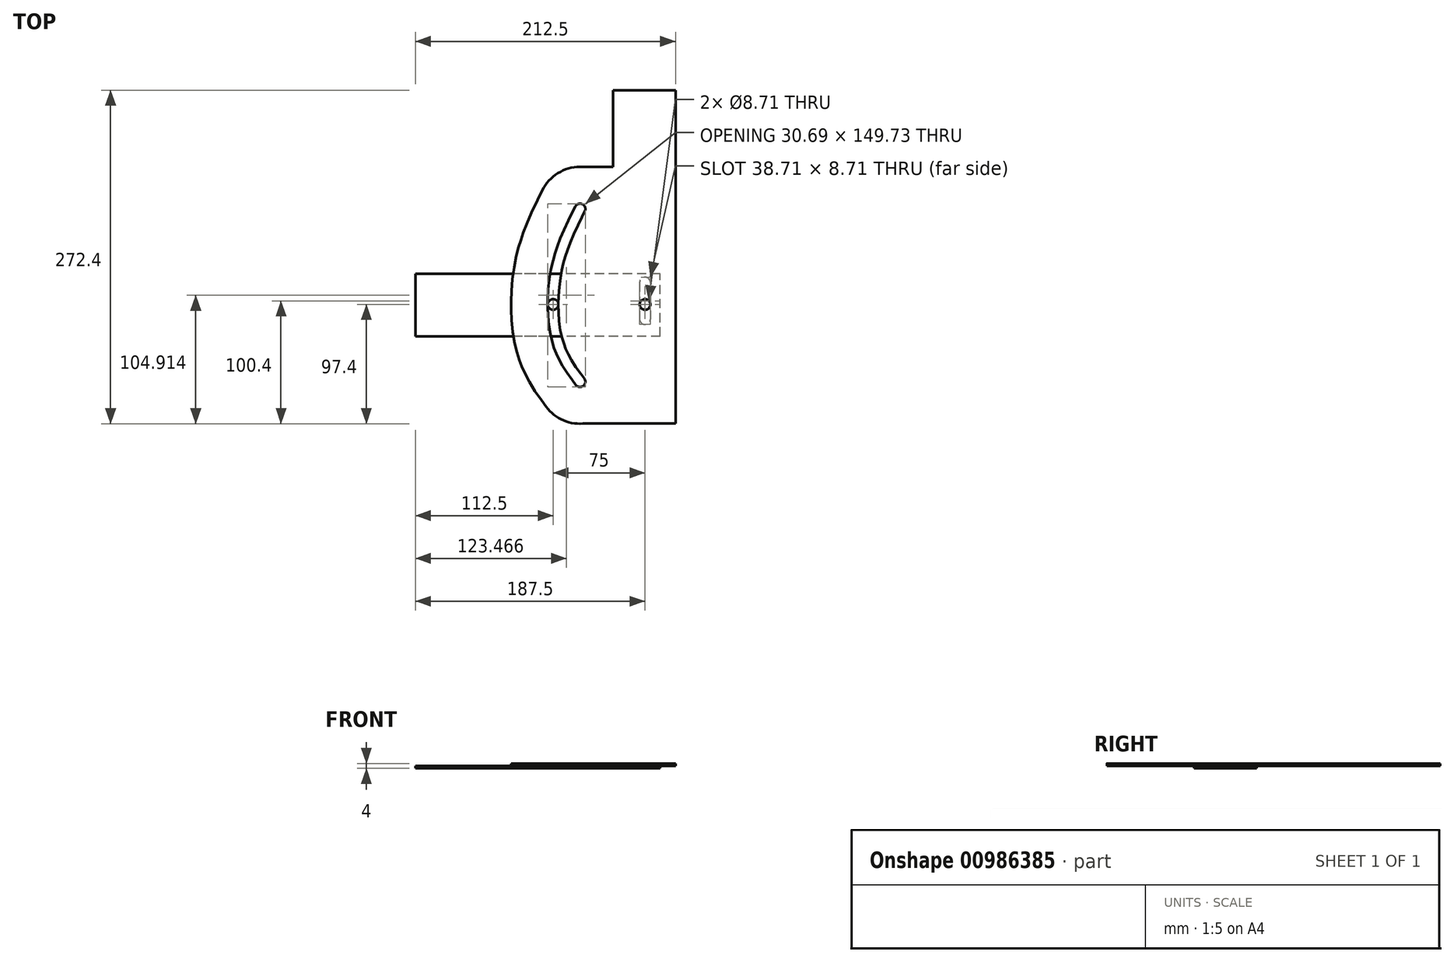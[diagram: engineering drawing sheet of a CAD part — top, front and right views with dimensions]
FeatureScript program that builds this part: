
annotation { "Feature Type Name" : "Feature", "Feature Type Description" : "" }
export const myFeature = defineFeature(function(context is Context, id is Id, definition is map)
    precondition{}
    {
        {
            var Q0;
            Q0=qCreatedBy(makeId("Top.planeOp"),FACE);
            var sketch = newSketch(context, id + "F0", { "sketchPlane" : qUnion([Q0])});
            skLineSegment(sketch, "E0", {"start": v(0, 0) * mm, "end": v(-25, 0) * mm, "construction": true});
            skLineSegment(sketch, "E1", {"start": v(-25, 0) * mm, "end": v(-100, 0) * mm, "construction": true});
            skLineSegment(sketch, "E2", {"start": v(-100, 0) * mm, "end": v(-100, -25) * mm, "construction": true});
            skLineSegment(sketch, "E3", {"start": v(-25, 0) * mm, "end": v(-25, -25) * mm, "construction": true});
            skLineSegment(sketch, "E4", {"start": v(-11.47, 0.06) * mm, "end": v(-34.57, -9.5) * mm, "construction": true});
            skLineSegment(sketch, "E5", {"start": v(-34.57, -9.5) * mm, "end": v(-103.86, -38.2) * mm, "construction": true});
            skLineSegment(sketch, "E6", {"start": v(-103.86, -38.2) * mm, "end": v(-94.3, -61.3) * mm, "construction": true});
            skLineSegment(sketch, "E7", {"start": v(-34.57, -9.5) * mm, "end": v(-25, -32.6) * mm, "construction": true});
            skLineSegment(sketch, "E8", {"start": v(-25, 0.35) * mm, "end": v(-42.68, -17.33) * mm, "construction": true});
            skLineSegment(sketch, "E9", {"start": v(-42.68, -17.33) * mm, "end": v(-95.71, -70.37) * mm, "construction": true});
            skLineSegment(sketch, "E10", {"start": v(-95.71, -70.37) * mm, "end": v(-78.03, -88.04) * mm, "construction": true});
            skLineSegment(sketch, "E11", {"start": v(-42.68, -17.33) * mm, "end": v(-25, -35) * mm, "construction": true});
            skLineSegment(sketch, "E12", {"start": v(7.66, 0.08) * mm, "end": v(-15.43, 9.65) * mm, "construction": true});
            skLineSegment(sketch, "E13", {"start": v(-15.43, 9.65) * mm, "end": v(-84.72, 38.35) * mm, "construction": true});
            skLineSegment(sketch, "E14", {"start": v(-84.72, 38.35) * mm, "end": v(-94.3, 15.25) * mm, "construction": true});
            skLineSegment(sketch, "E15", {"start": v(-15.43, 9.65) * mm, "end": v(-25, -13.45) * mm, "construction": true});
            skLineSegment(sketch, "E16", {"start": v(10.36, 0) * mm, "end": v(-7.32, 17.68) * mm, "construction": true});
            skLineSegment(sketch, "E17", {"start": v(-7.32, 17.68) * mm, "end": v(-60.36, 70.71) * mm, "construction": true});
            skLineSegment(sketch, "E18", {"start": v(-60.36, 70.71) * mm, "end": v(-78.03, 53.03) * mm, "construction": true});
            skLineSegment(sketch, "E19", {"start": v(-7.32, 17.68) * mm, "end": v(-25, 0) * mm, "construction": true});
            skSolve(sketch);
        }
        {
            var Q0;
            Q0=qCreatedBy(makeId("Top.planeOp"),FACE);
            var sketch = newSketch(context, id + "F1", { "sketchPlane" : qUnion([Q0])});
            skLineSegment(sketch, "E20.0", {"start": v(-60.36, 70.71) * mm, "end": v(-78.03, 53.03) * mm, "construction": true});
            skLineSegment(sketch, "E20.1", {"start": v(-84.72, 38.35) * mm, "end": v(-94.3, 15.25) * mm, "construction": true});
            skLineSegment(sketch, "E20.2", {"start": v(-100, 0) * mm, "end": v(-100, -25) * mm, "construction": true});
            skLineSegment(sketch, "E20.3", {"start": v(-103.86, -38.2) * mm, "end": v(-94.3, -61.3) * mm, "construction": true});
            skLineSegment(sketch, "E20.4", {"start": v(-95.71, -70.37) * mm, "end": v(-78.03, -88.04) * mm, "construction": true});
            skFitSpline(sketch, "E21", {"points": [v(-78.03, 53.03) * mm, v(-94.3, 15.25) * mm, v(-100, -25) * mm, v(-94.3, -61.3) * mm, v(-78.03, -88.04) * mm], "startDerivative": vector(-70.37, -141.2) * mm, "endDerivative": vector(81.07, -109.93) * mm});
            skArc(sketch, "E22.0.startCap", {"start": v(-81.93, 54.98) * mm, "mid": v(-76.1, 56.93) * mm, "end": v(-74.14, 51.1) * mm});
            skArc(sketch, "E22.0.endCap", {"start": v(-74.53, -85.46) * mm, "mid": v(-75.45, -91.55) * mm, "end": v(-81.54, -90.63) * mm});
            skFitSpline(sketch, "E22.0.left", {"points": [v(-74.14, 51.1) * mm, v(-75.6, 48.15) * mm, v(-78.52, 42.29) * mm, v(-82.69, 33.52) * mm, v(-85.84, 26.17) * mm, v(-88.08, 20.25) * mm, v(-89.6, 15.78) * mm, v(-90.94, 11.27) * mm, v(-92.1, 6.7) * mm, v(-93.1, 2.06) * mm, v(-94.2, -4.16) * mm, v(-95.16, -12.02) * mm, v(-95.6, -19.93) * mm, v(-95.67, -26.24) * mm, v(-95.53, -32.5) * mm, v(-94.97, -40.18) * mm, v(-93.8, -47.53) * mm, v(-92.45, -53.11) * mm, v(-91.43, -56.46) * mm, v(-90.5, -59.05) * mm, v(-89.5, -61.58) * mm, v(-88.1, -64.66) * mm, v(-86.2, -68.25) * mm, v(-83.43, -72.93) * mm, v(-79.56, -78.63) * mm, v(-76.22, -83.17) * mm, v(-74.53, -85.46) * mm]});
            skFitSpline(sketch, "E22.0.right", {"points": [v(-81.93, 54.98) * mm, v(-83.4, 52.03) * mm, v(-86.34, 46.13) * mm, v(-90.61, 37.13) * mm, v(-93.9, 29.47) * mm, v(-96.27, 23.2) * mm, v(-97.9, 18.43) * mm, v(-99.34, 13.58) * mm, v(-101, 7.04) * mm, v(-102.62, -1.23) * mm, v(-103.84, -11.25) * mm, v(-104.31, -19.62) * mm, v(-104.38, -26.28) * mm, v(-104.24, -32.93) * mm, v(-103.63, -41.16) * mm, v(-102.36, -49.18) * mm, v(-100.86, -55.39) * mm, v(-99.71, -59.17) * mm, v(-98.66, -62.12) * mm, v(-97.5, -65.02) * mm, v(-95.91, -68.51) * mm, v(-93.8, -72.52) * mm, v(-90.75, -77.64) * mm, v(-86.64, -83.71) * mm, v(-83.23, -88.34) * mm, v(-81.54, -90.63) * mm]});
            skLineSegment(sketch, "E23", {"start": v(0, 0) * mm, "end": v(0, -109.96) * mm, "construction": true});
            skArc(sketch, "E24.0", {"start": v(-50.38, -67.65) * mm, "mid": v(-57.64, -115.7) * mm, "end": v(-105.68, -108.43) * mm});
            skFitSpline(sketch, "E24.1", {"points": [v(-108.78, 68.36) * mm, v(-110.25, 65.42) * mm, v(-113.28, 59.34) * mm, v(-117.15, 51.2) * mm, v(-120.18, 44.31) * mm, v(-122.02, 39.84) * mm, v(-123.45, 36.16) * mm, v(-124.48, 33.35) * mm, v(-125.49, 30.48) * mm, v(-126.3, 28.03) * mm, v(-126.92, 26.05) * mm, v(-127.52, 24.06) * mm, v(-128.24, 21.55) * mm, v(-129.04, 18.53) * mm, v(-130.02, 14.51) * mm, v(-131.1, 9.48) * mm, v(-132.17, 3.45) * mm, v(-133.01, -2.58) * mm, v(-133.65, -8.6) * mm, v(-134.08, -14.58) * mm, v(-134.29, -19.54) * mm, v(-134.35, -23.5) * mm, v(-134.36, -26.45) * mm, v(-134.32, -29.42) * mm, v(-134.2, -33.4) * mm, v(-133.92, -38.45) * mm, v(-133.34, -44.56) * mm, v(-132.5, -50.73) * mm, v(-131.53, -55.92) * mm, v(-130.59, -60.1) * mm, v(-129.78, -63.23) * mm, v(-128.88, -66.38) * mm, v(-128.04, -69) * mm, v(-127.3, -71.1) * mm, v(-126.73, -72.69) * mm, v(-126.12, -74.26) * mm, v(-125.28, -76.33) * mm, v(-124.18, -78.84) * mm, v(-122.8, -81.74) * mm, v(-121.4, -84.52) * mm, v(-119.46, -88.07) * mm, v(-116.98, -92.23) * mm, v(-114, -96.82) * mm, v(-111.08, -101.03) * mm, v(-108.28, -104.9) * mm, v(-106.53, -107.29) * mm, v(-105.68, -108.43) * mm]});
            skArc(sketch, "E24.2", {"start": v(-108.78, 68.36) * mm, "mid": v(-62.7, 83.78) * mm, "end": v(-47.28, 37.7) * mm});
            skLineSegment(sketch, "E25", {"start": v(-73.41, -122.09) * mm, "end": v(0, -122.09) * mm});
            skLineSegment(sketch, "E26", {"start": v(0, -122.09) * mm, "end": v(0, 0) * mm});
            skLineSegment(sketch, "E27", {"start": v(-78.04, 87.39) * mm, "end": v(0, 87.39) * mm});
            skLineSegment(sketch, "E28", {"start": v(0, 0) * mm, "end": v(0, 150) * mm});
            skLineSegment(sketch, "E29", {"start": v(0, 150) * mm, "end": v(-51, 150) * mm});
            skLineSegment(sketch, "E30", {"start": v(-51, 150) * mm, "end": v(-51, 87.39) * mm});
            skLineSegment(sketch, "E31.0", {"start": v(0, 0) * mm, "end": v(-25, 0) * mm, "construction": true});
            skLineSegment(sketch, "E32.0", {"start": v(-25, 0) * mm, "end": v(-25, -25) * mm, "construction": true});
            skCircle(sketch, "E33", {"center": v(-25, -25) * mm, "radius": 4.36 * mm});
            skSolve(sketch);
        }
        {
            var Q0;
            Q0 = qSketchRegion(id + "F1", true);
            extrude(context, id + "F2", {"entities" : qUnion([Q0]), "depth" : 2 * mm, "offsetDistance" : 25 * mm});
        }
        {
            var Q0;
            Q0=qCreatedBy(makeId("Top.planeOp"),FACE);
            var sketch = newSketch(context, id + "F3", { "sketchPlane" : qUnion([Q0])});
            skLineSegment(sketch, "E34", {"start": v(-25, 0) * mm, "end": v(-12.5, 0) * mm, "construction": true});
            skLineSegment(sketch, "E35", {"start": v(-12.5, 0) * mm, "end": v(-12.5, -51) * mm, "construction": true});
            skLineSegment(sketch, "E36.0", {"start": v(-100, 0) * mm, "end": v(-100, -25) * mm, "construction": true});
            skCircle(sketch, "E37", {"center": v(-100, -25) * mm, "radius": 4.36 * mm});
            skCircle(sketch, "E38", {"center": v(-25, -25) * mm, "radius": 4.36 * mm});
            skLineSegment(sketch, "E39.bottom", {"start": v(-12.5, -51) * mm, "end": v(-212.5, -51) * mm});
            skLineSegment(sketch, "E39.top", {"start": v(-12.5, 0) * mm, "end": v(-212.5, 0) * mm});
            skLineSegment(sketch, "E39.left", {"start": v(-12.5, -51) * mm, "end": v(-12.5, 0) * mm});
            skLineSegment(sketch, "E39.right", {"start": v(-212.5, -51) * mm, "end": v(-212.5, 0) * mm});
            skArc(sketch, "E40.0.endCap", {"start": v(-20.64, -25) * mm, "mid": v(-25, -29.36) * mm, "end": v(-29.36, -25) * mm, "construction": true});
            skLineSegment(sketch, "E41", {"start": v(-25, -25) * mm, "end": v(-25, -7) * mm, "construction": true});
            skLineSegment(sketch, "E42", {"start": v(-25, -7) * mm, "end": v(-25, -37) * mm});
            skArc(sketch, "E43.0.startCap", {"start": v(-29.36, -7) * mm, "mid": v(-25, -2.64) * mm, "end": v(-20.64, -7) * mm});
            skArc(sketch, "E43.0.endCap", {"start": v(-20.64, -37) * mm, "mid": v(-25, -41.36) * mm, "end": v(-29.36, -37) * mm});
            skLineSegment(sketch, "E43.0.left", {"start": v(-20.64, -7) * mm, "end": v(-20.64, -37) * mm});
            skLineSegment(sketch, "E43.0.right", {"start": v(-29.36, -7) * mm, "end": v(-29.36, -37) * mm});
            skSolve(sketch);
        }
        {
            var Q0;
            Q0 = qSketchRegion(id + "F3", true);
            extrude(context, id + "F4", {"entities" : qUnion([Q0]), "oppositeDirection" : true, "depth" : 2 * mm, "offsetDistance" : 25 * mm});
        }
    });
